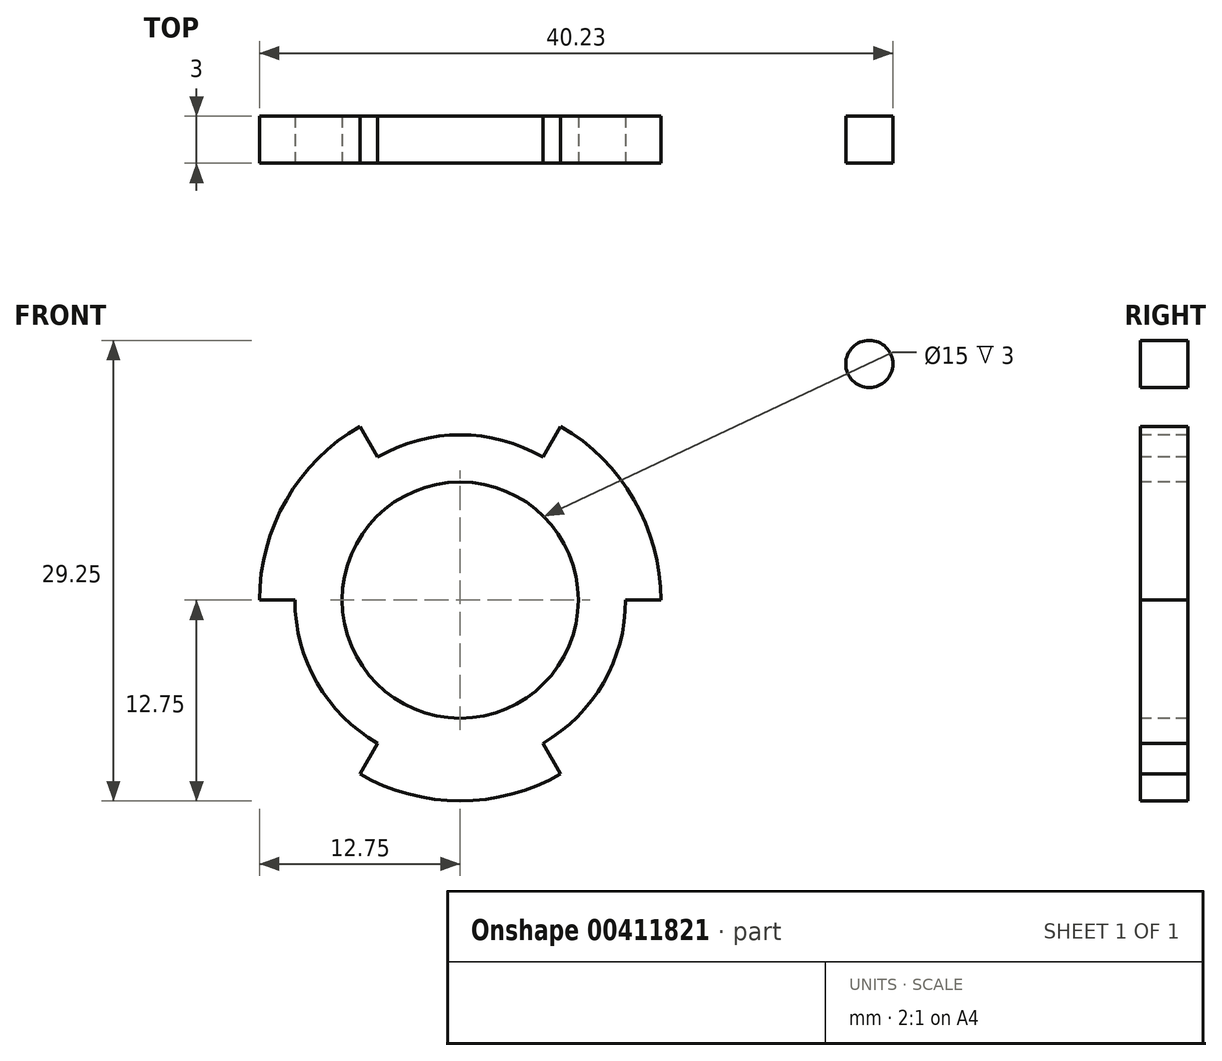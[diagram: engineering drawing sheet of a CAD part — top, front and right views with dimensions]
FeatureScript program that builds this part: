
annotation { "Feature Type Name" : "Feature", "Feature Type Description" : "" }
export const myFeature = defineFeature(function(context is Context, id is Id, definition is map)
    precondition{}
    {
        {
            var Q0;
            Q0=qCreatedBy(makeId("Front.planeOp"),FACE);
            var sketch = newSketch(context, id + "F0", { "sketchPlane" : qUnion([Q0])});
            skCircle(sketch, "E0", {"center": v(0, 0) * mm, "radius": 45 * mm, "construction": true});
            skLineSegment(sketch, "E1", {"start": v(0, 0) * mm, "end": v(-38.97, 22.5) * mm, "construction": true});
            skLineSegment(sketch, "E2.MirrorCS", {"start": v(0, 0) * mm, "end": v(38.97, 22.5) * mm, "construction": true});
            skLineSegment(sketch, "E3", {"start": v(0, 0) * mm, "end": v(0, -45) * mm, "construction": true});
            skPoint(sketch, "E4", {"position": v(-25.98, 15) * mm});
            skPoint(sketch, "E5.MirrorP", {"position": v(25.98, 15) * mm});
            skPoint(sketch, "E6", {"position": v(0, -30) * mm});
            skCircle(sketch, "E7", {"center": v(-34.64, 20) * mm, "radius": 5 * mm, "construction": true});
            skCircle(sketch, "E8", {"center": v(0, -40) * mm, "radius": 5 * mm, "construction": true});
            skLineSegment(sketch, "E9", {"start": v(-34.64, 20) * mm, "end": v(-38.97, 17.5) * mm, "construction": true});
            skLineSegment(sketch, "E10.MirrorCS", {"start": v(34.64, 20) * mm, "end": v(38.97, 17.5) * mm, "construction": true});
            skLineSegment(sketch, "E11", {"start": v(0, -40) * mm, "end": v(4.33, -42.5) * mm, "construction": true});
            skLineSegment(sketch, "E12", {"start": v(0, 0) * mm, "end": v(-38.97, -22.5) * mm, "construction": true});
            skLineSegment(sketch, "E13", {"start": v(0, 0) * mm, "end": v(38.97, -22.5) * mm, "construction": true});
            skPoint(sketch, "E14", {"position": v(-17.32, -10) * mm});
            skPoint(sketch, "E15.MirrorP", {"position": v(17.32, -10) * mm});
            skLineSegment(sketch, "E16.MirrorCS", {"start": v(0, -40) * mm, "end": v(-4.33, -42.5) * mm, "construction": true});
            skArc(sketch, "E17", {"start": v(-4.33, -42.5) * mm, "mid": v(-17.32, -10) * mm, "end": v(-38.97, 17.5) * mm});
            skArc(sketch, "E18.MirrorCS", {"start": v(4.33, -42.5) * mm, "mid": v(17.32, -10) * mm, "end": v(38.97, 17.5) * mm});
            skArc(sketch, "E19", {"start": v(-4.33, -42.5) * mm, "mid": v(0, -45) * mm, "end": v(4.33, -42.5) * mm});
            skLineSegment(sketch, "E20", {"start": v(0, 0) * mm, "end": v(0, 45) * mm, "construction": true});
            skPoint(sketch, "E21", {"position": v(0, 20) * mm});
            skLineSegment(sketch, "E22", {"start": v(-34.64, 20) * mm, "end": v(-34.64, 25) * mm, "construction": true});
            skCircle(sketch, "E23.MirrorC", {"center": v(34.64, 20) * mm, "radius": 5 * mm, "construction": true});
            skLineSegment(sketch, "E24.MirrorCS", {"start": v(34.64, 20) * mm, "end": v(34.64, 25) * mm, "construction": true});
            skArc(sketch, "E25", {"start": v(-34.64, 25) * mm, "mid": v(0, 20) * mm, "end": v(34.64, 25) * mm});
            skArc(sketch, "E26", {"start": v(38.97, 17.5) * mm, "mid": v(38.97, 22.5) * mm, "end": v(34.64, 25) * mm});
            skArc(sketch, "E27", {"start": v(-34.64, 25) * mm, "mid": v(-38.97, 22.5) * mm, "end": v(-38.97, 17.5) * mm});
            skSolve(sketch);
        }
        {
            var Q0;
            Q0=makeQuery(id+"F0.imprint","IMPRINT",FACE,{"disambiguationData":[TD([[makeQuery(id+"F0.imprint","IMPRINT",EDGE,{"derivedFrom":sQuery(id+"F0.wireOp",EDGE,"E17")}),-1.0]])]});
            extrude(context, id + "F1", {"entities" : qUnion([Q0]), "depth" : 3 * mm});
        }
        {
            var Q0;
            Q0=makeQuery(id+"F1.opExtrude","CAP_FACE",FACE,{"disambiguationData":[OSD([sQuery(id+"F0.wireOp",EDGE,"E17"),sQuery(id+"F0.wireOp",EDGE,"E18.MirrorCS"),sQuery(id+"F0.wireOp",EDGE,"E19"),sQuery(id+"F0.wireOp",EDGE,"E25"),sQuery(id+"F0.wireOp",EDGE,"E26"),sQuery(id+"F0.wireOp",EDGE,"E27")])],"isStart":false});
            var sketch = newSketch(context, id + "F2", { "sketchPlane" : qUnion([Q0])});
            skLineSegment(sketch, "E28", {"start": v(0, 0) * mm, "end": v(-51.96, 30) * mm, "construction": true});
            skLineSegment(sketch, "E29", {"start": v(0, 0) * mm, "end": v(0, -58.48) * mm, "construction": true});
            skLineSegment(sketch, "E30.MirrorCS", {"start": v(0, 0) * mm, "end": v(51.96, 30) * mm, "construction": true});
            skPoint(sketch, "E31", {"position": v(-25.98, 15) * mm});
            skPoint(sketch, "E32.MirrorP", {"position": v(25.98, 15) * mm});
            skPoint(sketch, "E33", {"position": v(0, -30) * mm});
            skCircle(sketch, "E34", {"center": v(-25.98, 15) * mm, "radius": 1.5 * mm});
            skCircle(sketch, "E35", {"center": v(0, -30) * mm, "radius": 1.5 * mm});
            skCircle(sketch, "E36", {"center": v(0, 0) * mm, "radius": 7.5 * mm});
            skCircle(sketch, "E37.MirrorC", {"center": v(25.98, 15) * mm, "radius": 1.5 * mm});
            skCircle(sketch, "E38", {"center": v(0, 0) * mm, "radius": 12.75 * mm});
            skCircle(sketch, "E39", {"center": v(0, 0) * mm, "radius": 10.5 * mm});
            skLineSegment(sketch, "E40", {"start": v(0, 0) * mm, "end": v(6.37, 11.04) * mm, "construction": true});
            skLineSegment(sketch, "E41", {"start": v(0, 0) * mm, "end": v(-6.38, 11.04) * mm, "construction": true});
            skLineSegment(sketch, "E42", {"start": v(0, 0) * mm, "end": v(-12.75, 0) * mm, "construction": true});
            skLineSegment(sketch, "E43", {"start": v(0, 0) * mm, "end": v(-6.37, -11.04) * mm, "construction": true});
            skLineSegment(sketch, "E44", {"start": v(0, 0) * mm, "end": v(6.38, -11.04) * mm, "construction": true});
            skLineSegment(sketch, "E45", {"start": v(0, 0) * mm, "end": v(12.75, 0) * mm, "construction": true});
            skLineSegment(sketch, "E46", {"start": v(-5.25, -9.1) * mm, "end": v(-6.37, -11.04) * mm});
            skLineSegment(sketch, "E47", {"start": v(5.25, -9.1) * mm, "end": v(6.38, -11.04) * mm});
            skLineSegment(sketch, "E48", {"start": v(10.5, 0) * mm, "end": v(12.75, 0) * mm});
            skLineSegment(sketch, "E49", {"start": v(5.25, 9.1) * mm, "end": v(6.37, 11.04) * mm});
            skLineSegment(sketch, "E50", {"start": v(-6.38, 11.04) * mm, "end": v(-5.25, 9.1) * mm});
            skLineSegment(sketch, "E51", {"start": v(-10.5, 0) * mm, "end": v(-12.75, 0) * mm});
            skSolve(sketch);
        }
        {
            var Q0;
            Q0=makeQuery(id+"F2.imprint","IMPRINT",FACE,{"disambiguationData":[TD([[makeQuery(id+"F2.imprint","IMPRINT",EDGE,{"derivedFrom":sQuery(id+"F2.wireOp",EDGE,"E34")}),1.0]])]});
            var Q1;
            Q1=makeQuery(id+"F2.imprint","IMPRINT",FACE,{"disambiguationData":[TD([[makeQuery(id+"F2.imprint","IMPRINT",EDGE,{"derivedFrom":sQuery(id+"F2.wireOp",EDGE,"E36")}),1.0]])]});
            var Q2;
            Q2=makeQuery(id+"F2.imprint","IMPRINT",FACE,{"disambiguationData":[TD([[makeQuery(id+"F2.imprint","IMPRINT",EDGE,{"derivedFrom":sQuery(id+"F2.wireOp",EDGE,"E37.MirrorC")}),-1.0]])]});
            var Q3;
            Q3=makeQuery(id+"F2.imprint","IMPRINT",FACE,{"disambiguationData":[TD([[makeQuery(id+"F2.imprint","IMPRINT",EDGE,{"derivedFrom":sQuery(id+"F2.wireOp",EDGE,"E35")}),1.0]])]});
            var Q4;
            {var subQ0=sQuery(id+"F2.wireOp",EDGE,"E49");Q4=makeQuery(id+"F2.imprint","IMPRINT",FACE,{"disambiguationData":[TD([[makeQuery(id+"F2.imprint","IMPRINT",EDGE,{"derivedFrom":subQ0}),1.0]])]});}
            var Q5;
            {var subQ0=sQuery(id+"F2.wireOp",EDGE,"E47");Q5=makeQuery(id+"F2.imprint","IMPRINT",FACE,{"disambiguationData":[TD([[makeQuery(id+"F2.imprint","IMPRINT",EDGE,{"derivedFrom":subQ0}),1.0]])]});}
            var Q6;
            {var subQ0=sQuery(id+"F2.wireOp",EDGE,"E46");Q6=makeQuery(id+"F2.imprint","IMPRINT",FACE,{"disambiguationData":[TD([[makeQuery(id+"F2.imprint","IMPRINT",EDGE,{"derivedFrom":subQ0}),-1.0]])]});}
            extrude(context, id + "F3", {"entities" : qUnion([Q0, Q1, Q2, Q3, Q4, Q5, Q6]), "operationType" : NewBodyOperationType.REMOVE, "endBound" : BoundingType.THROUGH_ALL, "oppositeDirection" : true, "depth" : 25 * mm});
        }
    });
